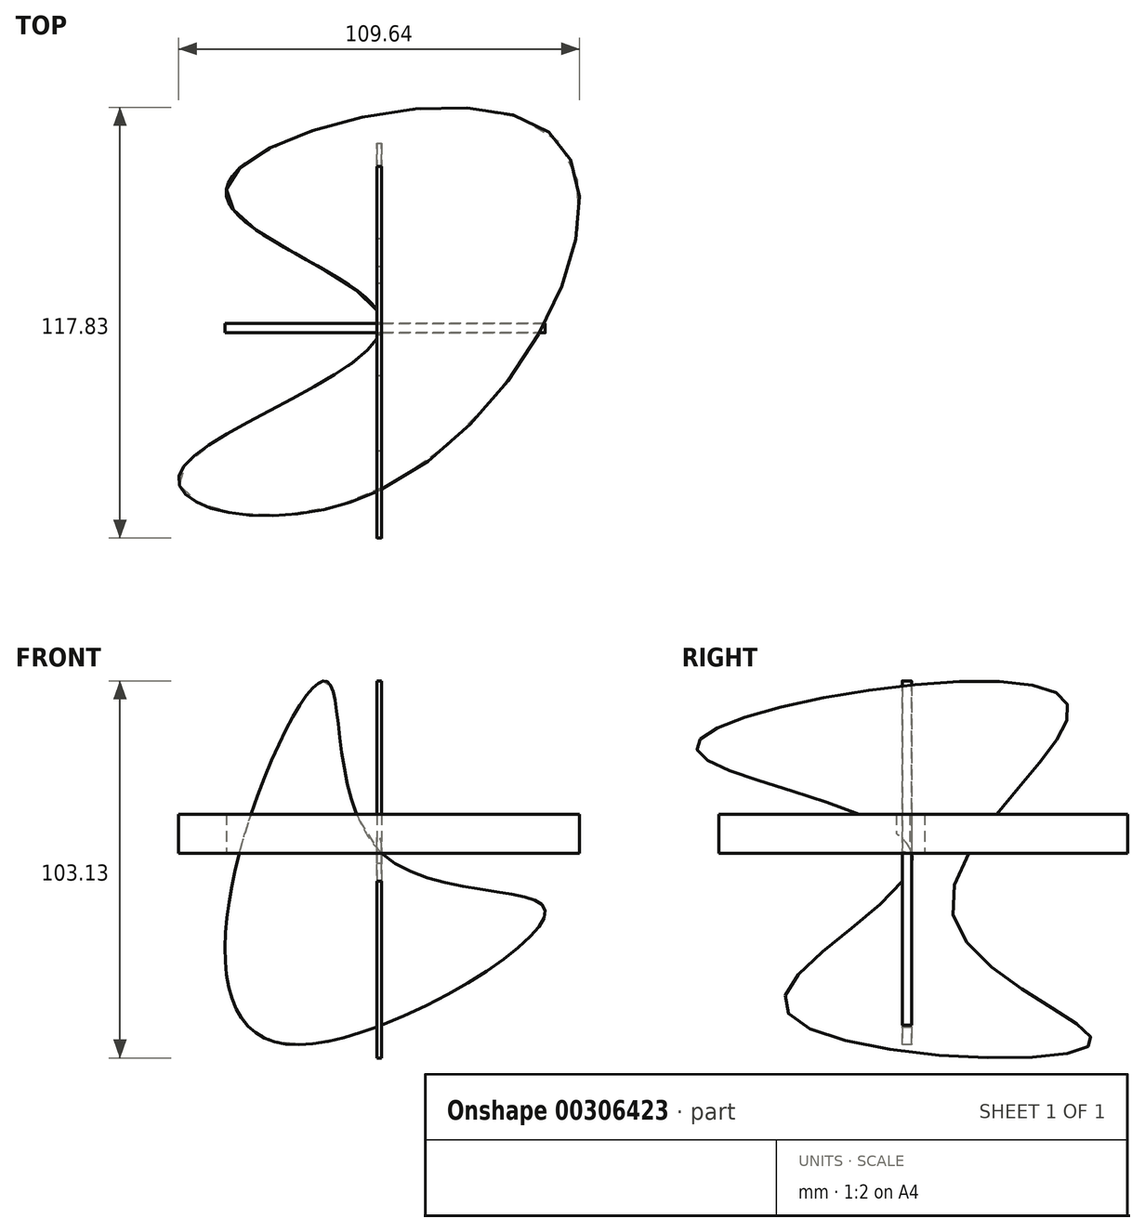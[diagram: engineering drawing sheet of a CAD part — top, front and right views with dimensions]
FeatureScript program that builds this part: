
annotation { "Feature Type Name" : "Feature", "Feature Type Description" : "" }
export const myFeature = defineFeature(function(context is Context, id is Id, definition is map)
    precondition{}
    {
        {
            var Q0;
            Q0=qCreatedBy(makeId("Front.planeOp"),FACE);
            var sketch = newSketch(context, id + "F0", { "sketchPlane" : qUnion([Q0])});
            skFitSpline(sketch, "E0", {"points": [v(0, 0) * mm, v(44.68, -15.85) * mm, v(-25.94, -52.24) * mm, v(-40, -4.32) * mm, v(-14.77, 46.84) * mm, v(0, 0) * mm]});
            skSolve(sketch);
        }
        {
            var Q0;
            Q0 = qSketchRegion(id + "F0", true);
            extrude(context, id + "F1", {"entities" : qUnion([Q0]), "depth" : 2.54 * mm});
        }
        {
            var Q0;
            Q0=qCreatedBy(makeId("Right.planeOp"),FACE);
            var sketch = newSketch(context, id + "F2", { "sketchPlane" : qUnion([Q0])});
            skFitSpline(sketch, "E1", {"points": [v(0, 0) * mm, v(-58.73, 29.18) * mm, v(41.8, 42.15) * mm, v(11.17, -15.85) * mm, v(49, -52.24) * mm, v(-34.59, -42.15) * mm, v(0, 0) * mm]});
            skSolve(sketch);
        }
        {
            var Q0;
            Q0 = qSketchRegion(id + "F2", true);
            extrude(context, id + "F3", {"entities" : qUnion([Q0]), "operationType" : NewBodyOperationType.ADD, "oppositeDirection" : true, "depth" : 1.27 * mm});
        }
        {
            var Q0;
            Q0=qCreatedBy(makeId("Top.planeOp"),FACE);
            var sketch = newSketch(context, id + "F4", { "sketchPlane" : qUnion([Q0])});
            skFitSpline(sketch, "E2", {"points": [v(0, 0) * mm, v(-42.51, 35.67) * mm, v(45.76, 52.24) * mm, v(0, -45.4) * mm, v(-55.12, -40.71) * mm, v(0, 0) * mm]});
            skSolve(sketch);
        }
        {
            var Q0;
            Q0 = qSketchRegion(id + "F4", true);
            extrude(context, id + "F5", {"entities" : qUnion([Q0]), "operationType" : NewBodyOperationType.ADD, "depth" : 10.67 * mm});
        }
    });
